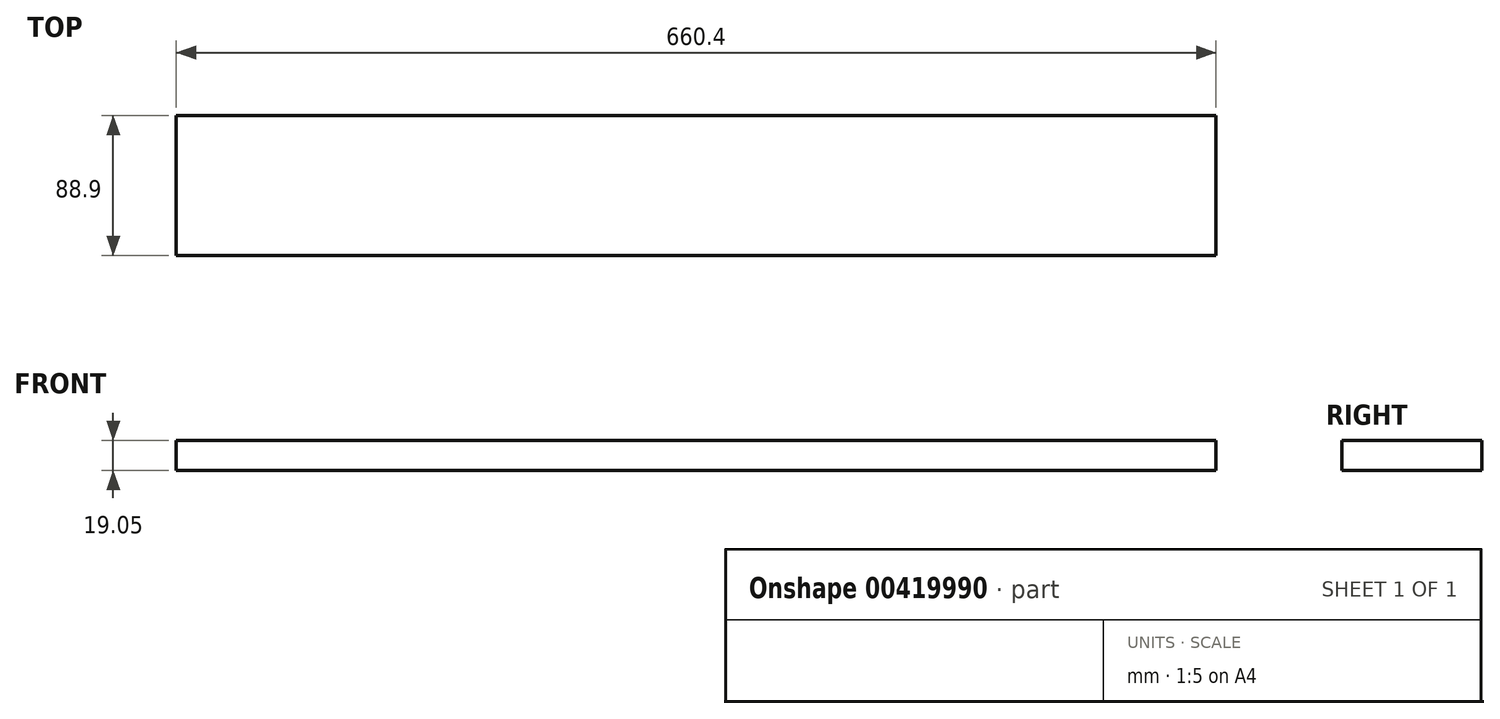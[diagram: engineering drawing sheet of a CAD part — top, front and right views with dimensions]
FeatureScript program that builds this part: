
annotation { "Feature Type Name" : "Feature", "Feature Type Description" : "" }
export const myFeature = defineFeature(function(context is Context, id is Id, definition is map)
    precondition{}
    {
        {
            var Q0;
            Q0=qCreatedBy(makeId("Top.planeOp"),FACE);
            var sketch = newSketch(context, id + "F0", { "sketchPlane" : qUnion([Q0])});
            skLineSegment(sketch, "E0.bottom", {"start": v(0, 0) * mm, "end": v(660.4, 0) * mm});
            skLineSegment(sketch, "E0.top", {"start": v(0, 88.9) * mm, "end": v(660.4, 88.9) * mm});
            skLineSegment(sketch, "E0.left", {"start": v(0, 0) * mm, "end": v(0, 88.9) * mm});
            skLineSegment(sketch, "E0.right", {"start": v(660.4, 0) * mm, "end": v(660.4, 88.9) * mm});
            skSolve(sketch);
        }
        {
            var Q0;
            Q0=makeQuery(id+"F0.imprint","IMPRINT",FACE,{"disambiguationData":[TD([[makeQuery(id+"F0.imprint","IMPRINT",EDGE,{"derivedFrom":sQuery(id+"F0.wireOp",EDGE,"E0.bottom")}),1.0]])]});
            extrude(context, id + "F1", {"entities" : qUnion([Q0]), "depth" : 19.05 * mm});
        }
    });
